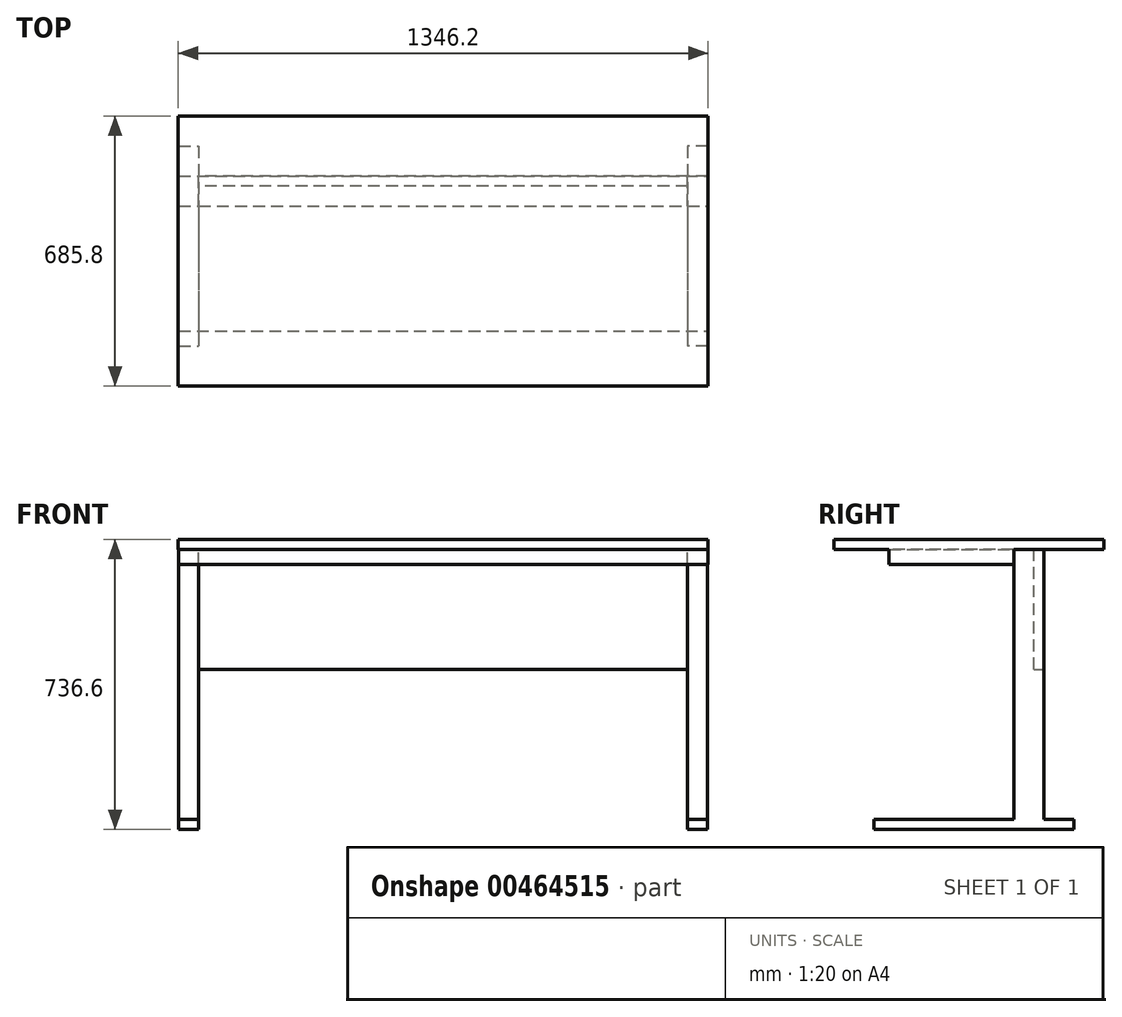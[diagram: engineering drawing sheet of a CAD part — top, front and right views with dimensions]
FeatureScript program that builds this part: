
annotation { "Feature Type Name" : "Feature", "Feature Type Description" : "" }
export const myFeature = defineFeature(function(context is Context, id is Id, definition is map)
    precondition{}
    {
        {
            var Q0;
            Q0=qCreatedBy(makeId("Top.planeOp"),FACE);
            var sketch = newSketch(context, id + "F0", { "sketchPlane" : qUnion([Q0])});
            skLineSegment(sketch, "E0.bottom", {"start": v(-670.92, 375.62) * mm, "end": v(675.28, 375.62) * mm});
            skLineSegment(sketch, "E0.top", {"start": v(-670.92, -310.18) * mm, "end": v(675.28, -310.18) * mm});
            skLineSegment(sketch, "E0.left", {"start": v(-670.92, 375.62) * mm, "end": v(-670.92, -310.18) * mm});
            skLineSegment(sketch, "E0.right", {"start": v(675.28, 375.62) * mm, "end": v(675.28, -310.18) * mm});
            skSolve(sketch);
        }
        {
            var Q0;
            Q0 = qSketchRegion(id + "F0", true);
            extrude(context, id + "F1", {"entities" : qUnion([Q0]), "depth" : 25.4 * mm});
        }
        {
            var Q0;
            Q0=qCreatedBy(makeId("Top.planeOp"),FACE);
            var sketch = newSketch(context, id + "F2", { "sketchPlane" : qUnion([Q0])});
            skLineSegment(sketch, "E1.bottom", {"start": v(-669.37, 147.02) * mm, "end": v(-618.57, 147.02) * mm});
            skLineSegment(sketch, "E1.top", {"start": v(-669.37, 223.22) * mm, "end": v(-618.57, 223.22) * mm});
            skLineSegment(sketch, "E1.left", {"start": v(-669.37, 147.02) * mm, "end": v(-669.37, 223.22) * mm});
            skLineSegment(sketch, "E1.right", {"start": v(-618.57, 147.02) * mm, "end": v(-618.57, 223.22) * mm});
            skLineSegment(sketch, "E2.bottom", {"start": v(673.97, 147.02) * mm, "end": v(623.17, 147.02) * mm});
            skLineSegment(sketch, "E2.top", {"start": v(673.97, 223.22) * mm, "end": v(623.17, 223.22) * mm});
            skLineSegment(sketch, "E2.left", {"start": v(673.97, 147.02) * mm, "end": v(673.97, 223.22) * mm});
            skLineSegment(sketch, "E2.right", {"start": v(623.17, 147.02) * mm, "end": v(623.17, 223.22) * mm});
            skSolve(sketch);
        }
        {
            var Q0;
            Q0 = qSketchRegion(id + "F2", true);
            extrude(context, id + "F3", {"entities" : qUnion([Q0]), "oppositeDirection" : true, "depth" : 685.8 * mm});
        }
        {
            var Q0;
            Q0=makeQuery(id+"F1.opExtrude","CAP_FACE",FACE,{"disambiguationData":[OSD([sQuery(id+"F0.wireOp",EDGE,"E0.bottom"),sQuery(id+"F0.wireOp",EDGE,"E0.top"),sQuery(id+"F0.wireOp",EDGE,"E0.left"),sQuery(id+"F0.wireOp",EDGE,"E0.right")])],"isStart":true});
            var sketch = newSketch(context, id + "F4", { "sketchPlane" : qUnion([Q0])});
            skLineSegment(sketch, "E3.bottom", {"start": v(-669.37, -147.02) * mm, "end": v(675.28, -147.02) * mm});
            skLineSegment(sketch, "E3.top", {"start": v(-669.37, 170.48) * mm, "end": v(675.28, 170.48) * mm});
            skLineSegment(sketch, "E3.left", {"start": v(-669.37, -147.02) * mm, "end": v(-669.37, 170.48) * mm});
            skLineSegment(sketch, "E3.right", {"start": v(675.28, -147.02) * mm, "end": v(675.28, 170.48) * mm});
            skSolve(sketch);
        }
        {
            var Q0;
            Q0 = qSketchRegion(id + "F4", true);
            extrude(context, id + "F5", {"entities" : qUnion([Q0]), "operationType" : NewBodyOperationType.ADD, "depth" : 38.1 * mm});
        }
        {
            var Q0;
            Q0=makeQuery(id+"F3.opExtrude","SWEPT_FACE",FACE,{"disambiguationData":[OSD([sQuery(id+"F2.wireOp",EDGE,"E2.top")])]});
            var sketch = newSketch(context, id + "F6", { "sketchPlane" : qUnion([Q0])});
            skLineSegment(sketch, "E4.bottom", {"start": v(-673.97, -685.8) * mm, "end": v(-623.17, -685.8) * mm});
            skLineSegment(sketch, "E4.top", {"start": v(-673.97, -711.2) * mm, "end": v(-623.17, -711.2) * mm});
            skLineSegment(sketch, "E4.left", {"start": v(-673.97, -685.8) * mm, "end": v(-673.97, -711.2) * mm});
            skLineSegment(sketch, "E4.right", {"start": v(-623.17, -685.8) * mm, "end": v(-623.17, -711.2) * mm});
            skLineSegment(sketch, "E5.bottom", {"start": v(-623.17, -685.8) * mm, "end": v(-623.17, -685.8) * mm});
            skLineSegment(sketch, "E5.top", {"start": v(-623.17, -685.8) * mm, "end": v(-623.17, -685.8) * mm});
            skLineSegment(sketch, "E5.left", {"start": v(-623.17, -685.8) * mm, "end": v(-623.17, -685.8) * mm});
            skLineSegment(sketch, "E5.right", {"start": v(-623.17, -685.8) * mm, "end": v(-623.17, -685.8) * mm});
            skSolve(sketch);
        }
        {
            var Q0;
            Q0=makeQuery(id+"F3.opExtrude","SWEPT_FACE",FACE,{"disambiguationData":[OSD([sQuery(id+"F2.wireOp",EDGE,"E1.top")])]});
            var sketch = newSketch(context, id + "F7", { "sketchPlane" : qUnion([Q0])});
            skLineSegment(sketch, "E6.bottom", {"start": v(618.57, -685.8) * mm, "end": v(669.37, -685.8) * mm});
            skLineSegment(sketch, "E6.top", {"start": v(618.57, -711.2) * mm, "end": v(669.37, -711.2) * mm});
            skLineSegment(sketch, "E6.left", {"start": v(618.57, -685.8) * mm, "end": v(618.57, -711.2) * mm});
            skLineSegment(sketch, "E6.right", {"start": v(669.37, -685.8) * mm, "end": v(669.37, -711.2) * mm});
            skSolve(sketch);
        }
        {
            var Q0;
            Q0 = qSketchRegion(id + "F6", true);
            extrude(context, id + "F8", {"entities" : qUnion([Q0]), "operationType" : NewBodyOperationType.ADD, "depth" : 76.2 * mm, "hasSecondDirection" : true, "secondDirectionOppositeDirection" : true, "secondDirectionDepth" : 431.8 * mm});
        }
        {
            var Q0;
            Q0 = qSketchRegion(id + "F7", true);
            extrude(context, id + "F9", {"entities" : qUnion([Q0]), "operationType" : NewBodyOperationType.ADD, "depth" : 76.2 * mm, "hasSecondDirection" : true, "secondDirectionOppositeDirection" : true, "secondDirectionDepth" : 431.8 * mm});
        }
        {
            var Q0;
            Q0=makeQuery(id+"F3.opExtrude","SWEPT_FACE",FACE,{"disambiguationData":[OSD([sQuery(id+"F2.wireOp",EDGE,"E2.top")])]});
            var sketch = newSketch(context, id + "F10", { "sketchPlane" : qUnion([Q0])});
            skLineSegment(sketch, "E7.bottom", {"start": v(-623.17, 0) * mm, "end": v(621.43, 0) * mm});
            skLineSegment(sketch, "E7.top", {"start": v(-623.17, -304.8) * mm, "end": v(621.43, -304.8) * mm});
            skLineSegment(sketch, "E7.left", {"start": v(-623.17, 0) * mm, "end": v(-623.17, -304.8) * mm});
            skLineSegment(sketch, "E7.right", {"start": v(621.43, 0) * mm, "end": v(621.43, -304.8) * mm});
            skSolve(sketch);
        }
        {
            var Q0;
            Q0=makeQuery(id+"F10.imprint","IMPRINT",FACE,{"disambiguationData":[TD([[makeQuery(id+"F10.imprint","IMPRINT",EDGE,{"derivedFrom":sQuery(id+"F10.wireOp",EDGE,"E7.bottom")}),-1.0]])]});
            extrude(context, id + "F11", {"entities" : qUnion([Q0]), "operationType" : NewBodyOperationType.ADD, "oppositeDirection" : true, "depth" : 25.4 * mm});
        }
    });
